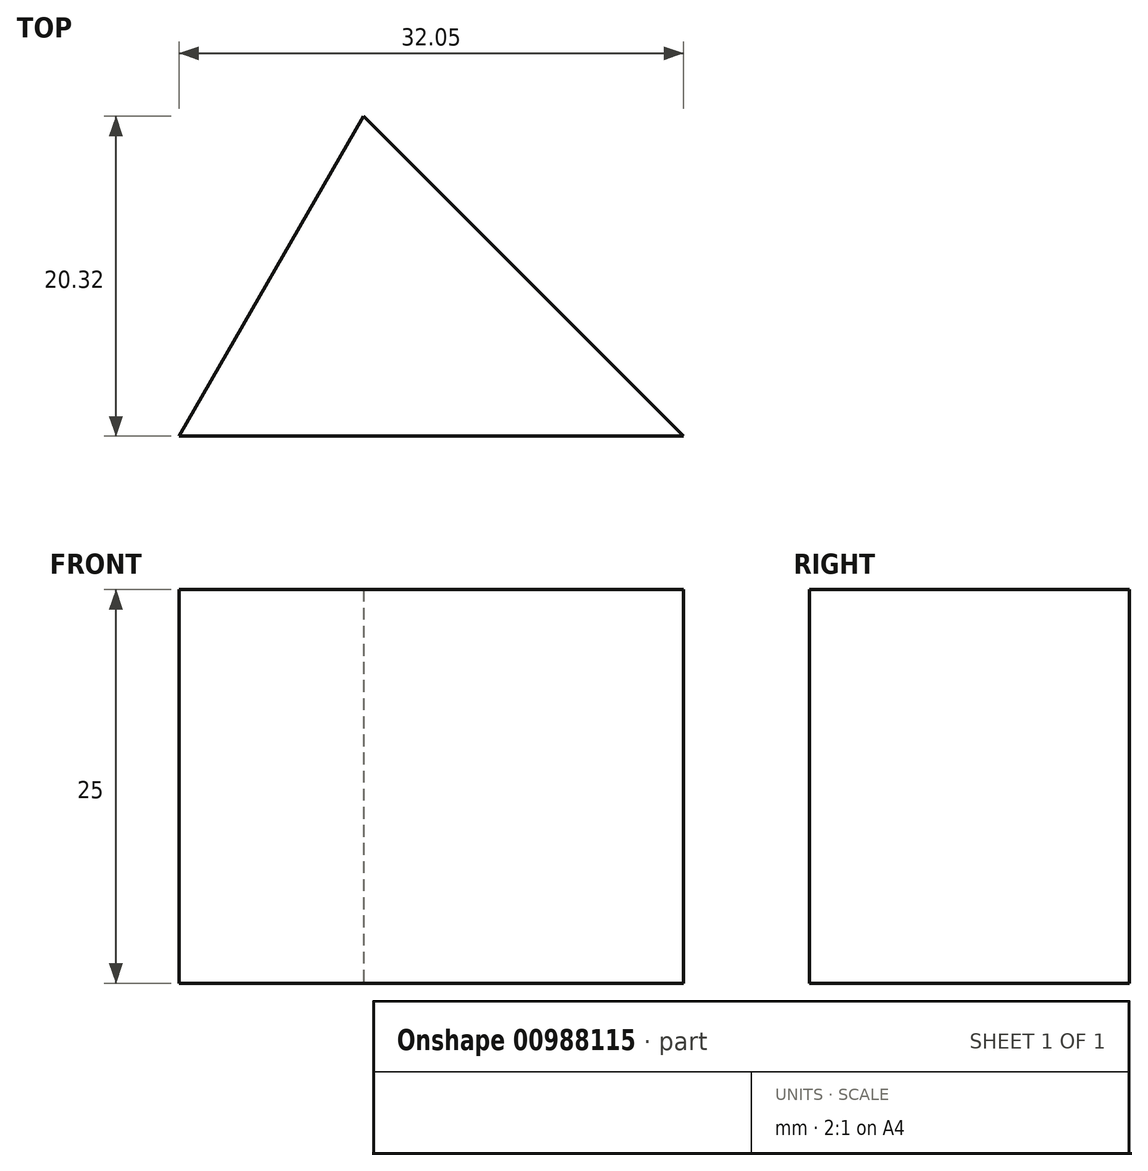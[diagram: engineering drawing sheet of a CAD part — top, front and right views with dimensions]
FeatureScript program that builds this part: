
annotation { "Feature Type Name" : "Feature", "Feature Type Description" : "" }
export const myFeature = defineFeature(function(context is Context, id is Id, definition is map)
    precondition{}
    {
        {
            var Q0;
            Q0=qCreatedBy(makeId("Top.planeOp"),FACE);
            var sketch = newSketch(context, id + "F0", { "sketchPlane" : qUnion([Q0])});
            skLineSegment(sketch, "E0", {"start": v(1.2, 0) * mm, "end": v(12.93, 20.32) * mm});
            skLineSegment(sketch, "E1", {"start": v(12.93, 20.32) * mm, "end": v(33.25, 0) * mm});
            skLineSegment(sketch, "E2", {"start": v(33.25, 0) * mm, "end": v(1.2, 0) * mm});
            skSolve(sketch);
        }
        {
            var Q0;
            Q0 = qSketchRegion(id + "F0", true);
            extrude(context, id + "F1", {"entities" : qUnion([Q0]), "depth" : 25 * mm, "offsetDistance" : 25 * mm});
        }
    });
